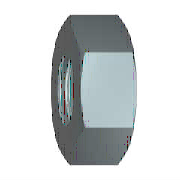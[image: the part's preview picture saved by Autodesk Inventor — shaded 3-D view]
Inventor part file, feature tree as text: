
AUTODESK INVENTOR PART (.ipt)
format: ipt  version: 2020 (Build 240168000, 168)  size: 166,400 bytes
history: native  units: mm (DEFAULTED — no unit token found)
features: sketch x3, other x2, extrude x1, hole x1, plane x1
ambient origin geometry x7: Origin, YZ Plane, XZ Plane, X Axis, Y Axis, Z Axis, Center Point
bodies: Solid1 (feature_tree)
feature tree (8):
  extrude  "Bryła"  Depth=9.237604mm
  other  "Faza1"
  hole  "Gwint"  [1 undecoded]
  other  "Work Axis1"
  plane  "Work Plane1"
  sketch  "Szkic1"
  sketch  "Szkic2"
  sketch  "Szkic3"
note: 1 required parameter value undecoded (feature->parameter linkage not recoverable at this tier; creation-order binding heuristic only, values carry confidence <= 0.55)
